# Revit family: StructuralFraming_LightWeight_Lindab_LTP20
name_source: partatom
category: Structural Framing
revit_build: Autodesk Revit Architecture 2016 (Build: 20150220_1215(x64)
units: mm (PartAtom-declared; Revit-internal decimal feet)

## family parameters
Always export as geometry = No
Always vertical = Yes
Cut with Voids When Loaded = No
Material for Model Behavior = Steel
OmniClass Number = 23.25.30.11.14.14
OmniClass Title = Beams
Section Shape = Not Defined
Shared = No
Show family pre-cut in plan views = Yes

## types (1)
- StructuralFraming_LightWeight_Lindab_LTP20
    Advanced_Design_Tool = http://www.lindab.com
    Covering_Width = 1035 mm  [stored 3.39567 ft]
    FamilyVersion = 1.0
    Height = 18 mm  [stored 0.0590551 ft]
    LindabRevitLibrary_Tool = http://www.lindab.com
    Manufacturer = Lindab
    Quick_Design_Tool = http://structuraldesigner.lindab.com
    Section_Properties_Tool = http://ec3library.lindab.com
    Structural Material = Lindab_015_Black
    Thickness = 0.7 mm  [stored 0.00229659 ft]
    URL = www.lindab.com
    Wave_Length = 115 mm  [stored 0.377297 ft]

note: [stored X ft] marks values corroborated as IEEE doubles in the binary element streams (Revit-internal decimal feet)

## geometry (parser evidence)
native form markers: Sweep x3
no freeform markers — native parametric forms only
